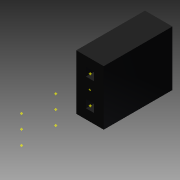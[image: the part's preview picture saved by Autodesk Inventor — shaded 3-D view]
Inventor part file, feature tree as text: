
AUTODESK INVENTOR PART (.ipt)
format: ipt  version: 2011 (Build 150239000, 239)  size: 83,968 bytes
history: native  units: in
note: dims shown in document units (in); Inventor stores cm internally (conversion verified against a paired STEP export)
features: other x12, plane x6, extrude x1, sketch x1
ambient origin geometry x8: Origin, YZ Plane, XZ Plane, XY Plane, X Axis, Y Axis, Z Axis, Center Point
bodies: Solid1 (feature_tree)
feature tree (20):
  extrude  "Extrusion1"  Depth=0.125in
  other  "Work Point8"
  other  "Work Point9"
  other  "Work Point10"
  other  "Work Point11"
  other  "Work Point13"
  other  "Work Point14"
  sketch  "Sketch1"  dims[d0=0.25in d1=0.0in d3=0.125in d4=0.25in d5=0.125in d6=0.25in d7=0.125in d8=0.25in]
  plane  "Work Plane6"
  other  "Work Axis6"
  plane  "Work Plane7"
  other  "Work Axis7"
  plane  "Work Plane8"
  other  "Work Axis8"
  plane  "Work Plane9"
  other  "Work Axis9"
  plane  "Work Plane10"
  other  "Work Axis10"
  plane  "Work Plane11"
  other  "Work Axis11"
